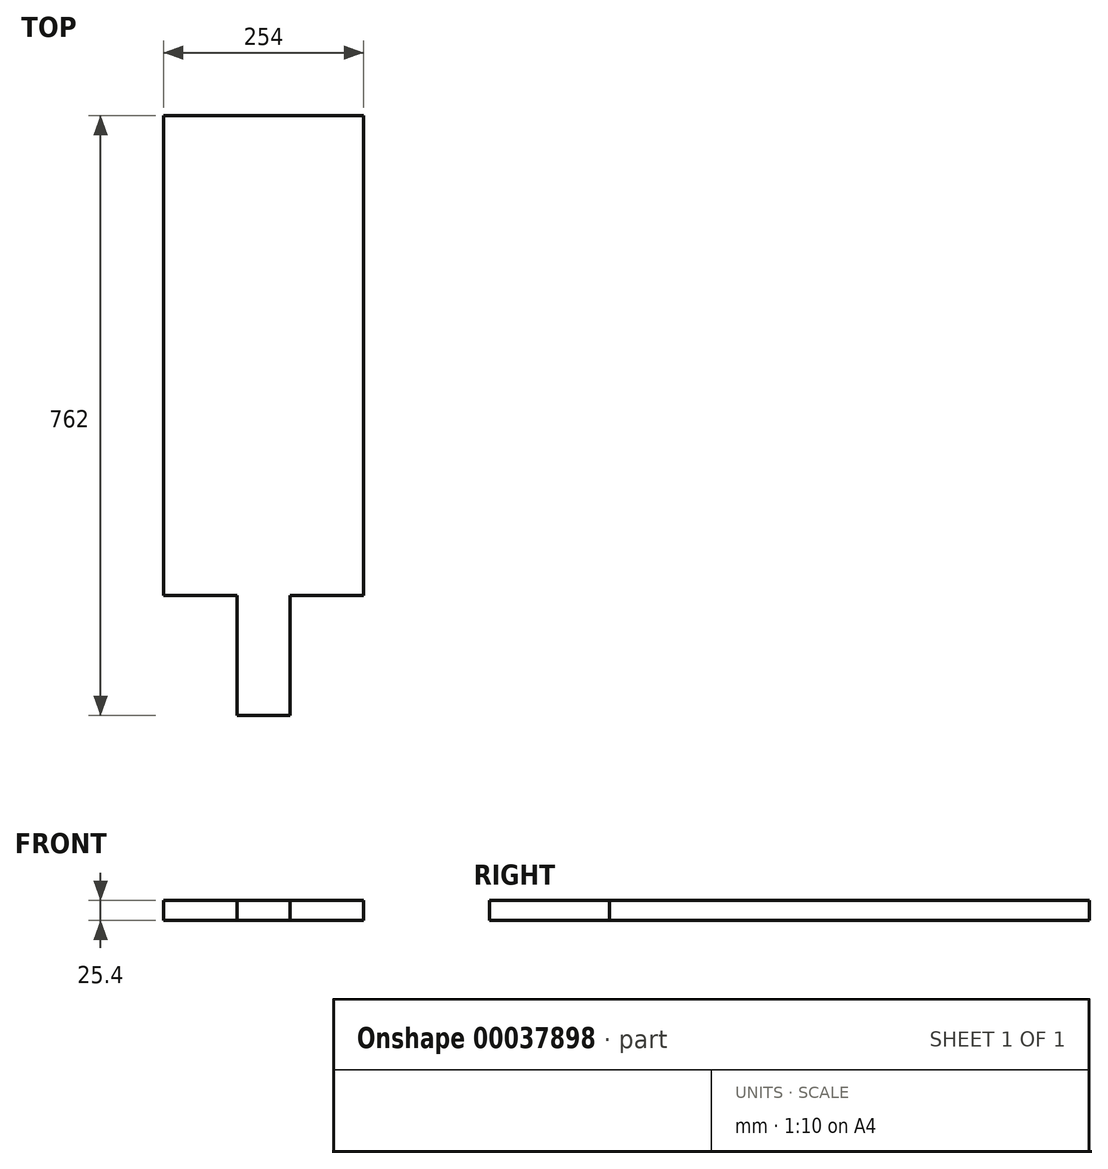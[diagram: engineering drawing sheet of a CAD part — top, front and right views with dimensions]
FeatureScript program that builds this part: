
annotation { "Feature Type Name" : "Feature", "Feature Type Description" : "" }
export const myFeature = defineFeature(function(context is Context, id is Id, definition is map)
    precondition{}
    {
        {
            var Q0;
            Q0=qCreatedBy(makeId("Top.planeOp"),FACE);
            var sketch = newSketch(context, id + "F0", { "sketchPlane" : qUnion([Q0])});
            skLineSegment(sketch, "E0.bottom", {"start": v(0, 0) * mm, "end": v(254, 0) * mm});
            skLineSegment(sketch, "E0.left", {"start": v(0, 0) * mm, "end": v(0, -609.6) * mm});
            skLineSegment(sketch, "E0.right", {"start": v(254, 0) * mm, "end": v(254, -609.6) * mm});
            skLineSegment(sketch, "E1", {"start": v(0, -609.6) * mm, "end": v(93.13, -609.6) * mm});
            skLineSegment(sketch, "E2", {"start": v(254, -609.6) * mm, "end": v(160.87, -609.6) * mm});
            skLineSegment(sketch, "E3", {"start": v(160.87, -609.6) * mm, "end": v(160.87, -762) * mm});
            skLineSegment(sketch, "E4", {"start": v(160.87, -762) * mm, "end": v(93.13, -762) * mm});
            skLineSegment(sketch, "E5", {"start": v(93.13, -609.6) * mm, "end": v(93.13, -762) * mm});
            skSolve(sketch);
        }
        {
            var Q0;
            Q0=qSketchRegion(id+"F0",true);
            extrude(context, id + "F1", {"entities" : qUnion([Q0]), "depth" : 25.4 * mm});
        }
    });
